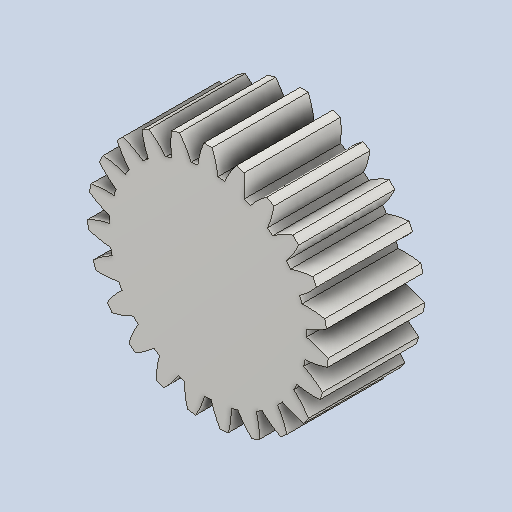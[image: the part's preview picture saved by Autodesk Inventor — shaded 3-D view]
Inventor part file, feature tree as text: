
AUTODESK INVENTOR PART (.ipt)
format: ipt  version: 2022 (Build 260153000, 153)  size: 268,288 bytes
history: native  units: mm (DEFAULTED — no unit token found)
features: plane x3, other x3, sketch x2, extrude x1
ambient origin geometry x8: Origin, YZ Plane, XZ Plane, XY Plane, X Axis, Y Axis, Z Axis, Center Point
bodies: Solid1 (feature_tree)
feature tree (9):
  extrude  "Extrusion1"  Depth=25.4mm TaperAngle=0.0deg
  plane  "Work Plane1"
  plane  "Work Plane2"
  plane  "Work Plane3"
  other  "Spur Gear"
  sketch  "Sketch1"  dims[d0=63.5mm d1=25.4mm d2=0.0mm]
  sketch  "Sketch2"  dims[d3=58.42mm d4=76.2mm d5=0.0mm d6=0.0mm d7=1.36591mm d9=0.0mm d14=0.0mm d15=101.6mm d16=0.0mm d17=0.0mm d18=0.0mm d19=101.6mm]
  other  "Srf1"
  other  "Pitch Diameter"
